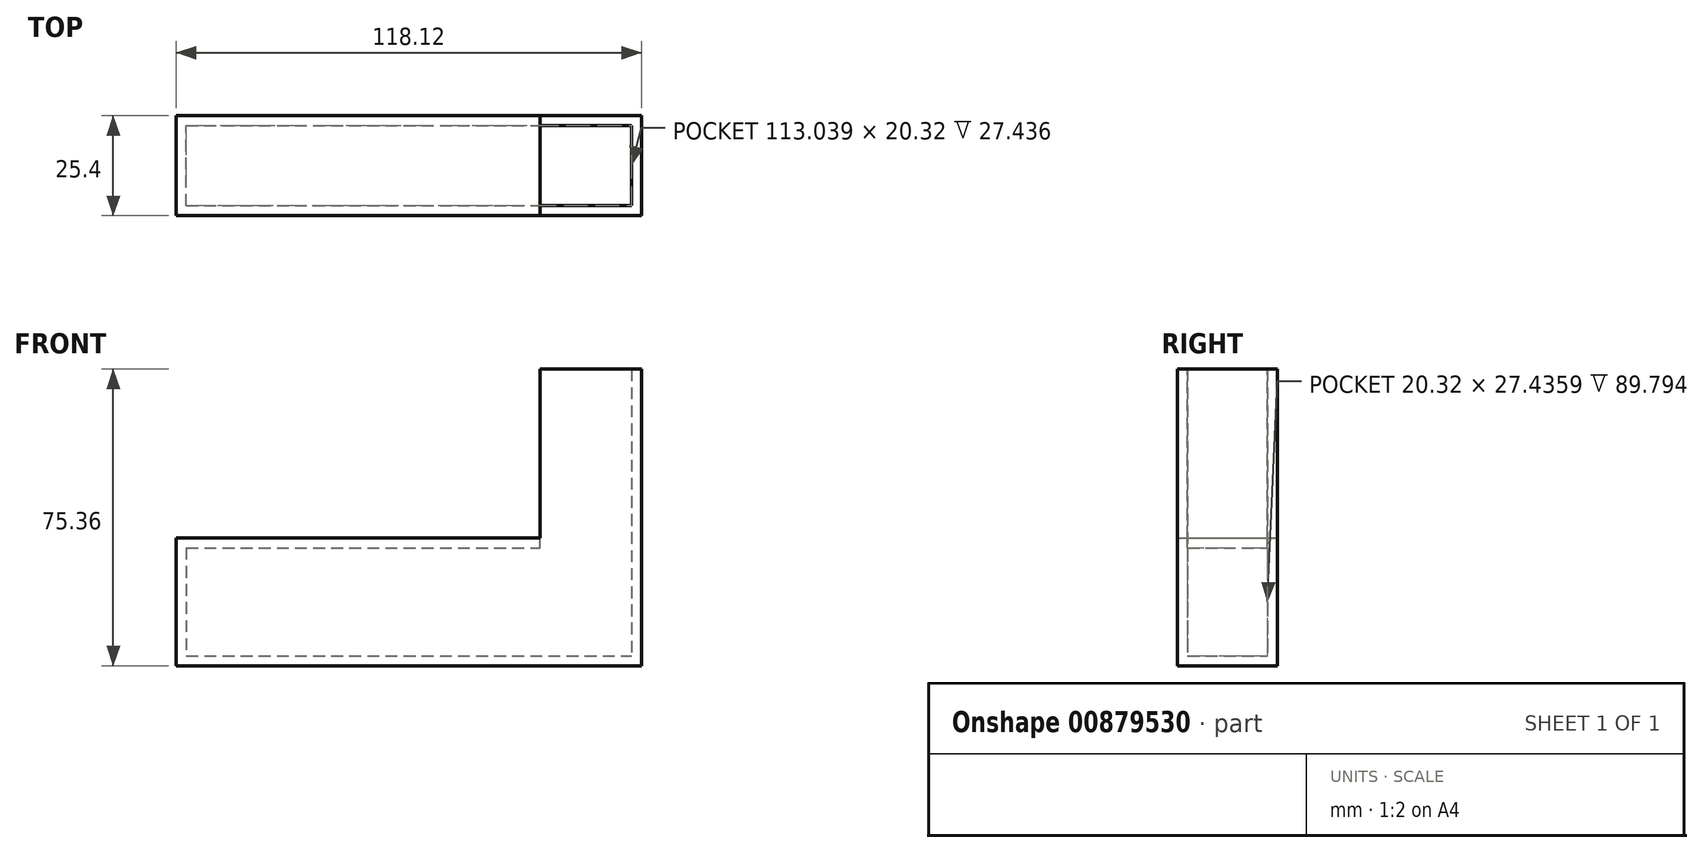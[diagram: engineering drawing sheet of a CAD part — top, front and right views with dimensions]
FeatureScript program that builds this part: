
annotation { "Feature Type Name" : "Feature", "Feature Type Description" : "" }
export const myFeature = defineFeature(function(context is Context, id is Id, definition is map)
    precondition{}
    {
        {
            var Q0;
            Q0=qCreatedBy(makeId("Front.planeOp"),FACE);
            var sketch = newSketch(context, id + "F0", { "sketchPlane" : qUnion([Q0])});
            skLineSegment(sketch, "E0.bottom", {"start": v(-56.22, 32.52) * mm, "end": v(61.9, 32.52) * mm});
            skLineSegment(sketch, "E0.top", {"start": v(-56.22, 0) * mm, "end": v(61.9, 0) * mm});
            skLineSegment(sketch, "E0.left", {"start": v(-56.22, 32.52) * mm, "end": v(-56.22, 0) * mm});
            skLineSegment(sketch, "E0.right", {"start": v(61.9, 32.52) * mm, "end": v(61.9, 0) * mm});
            skLineSegment(sketch, "E1", {"start": v(36.12, 32.52) * mm, "end": v(36.12, 49.96) * mm});
            skLineSegment(sketch, "E2", {"start": v(36.12, 49.96) * mm, "end": v(61.9, 49.96) * mm});
            skLineSegment(sketch, "E3", {"start": v(61.9, 49.96) * mm, "end": v(61.9, 32.52) * mm});
            skSolve(sketch);
        }
        {
            var Q0;
            Q0=makeQuery(id+"F0.imprint","IMPRINT",FACE,{"disambiguationData":[TD([[makeQuery(id+"F0.imprint","IMPRINT",EDGE,{"derivedFrom":sQuery(id+"F0.wireOp",EDGE,"E0.top")}),1.0]])]});
            var Q1;
            {var subQ2=sQuery(id+"F0.wireOp",EDGE,"E1");Q1=makeQuery(id+"F0.imprint","IMPRINT",FACE,{"disambiguationData":[TD([[makeQuery(id+"F0.imprint","IMPRINT",EDGE,{"derivedFrom":subQ2}),-1.0]])]});}
            extrude(context, id + "F1", {"entities" : qUnion([Q0, Q1]), "depth" : 25.4 * mm, "offsetDistance" : 25.4 * mm});
        }
        {
            var Q0;
            Q0=makeQuery(id+"F1.opExtrude","SWEPT_FACE",FACE,{"disambiguationData":[OSD([sQuery(id+"F0.wireOp",EDGE,"E2")])]});
            extrude(context, id + "F2", {"entities" : qUnion([Q0]), "operationType" : NewBodyOperationType.ADD, "depth" : 25.4 * mm, "offsetDistance" : 25.4 * mm});
        }
        {
            var Q0;
            Q0=makeQuery(id+"F2.opExtrude","CAP_FACE",FACE,{"disambiguationData":[OSD([sQuery(id+"F0.wireOp",EDGE,"E2")])],"isStart":false});
            var Q1;
            {var subQ0=sQuery(id+"F0.wireOp",EDGE,"E1");Q1=makeQuery(id+"F2.boolean.opBoolean","MERGE",FACE,{"derivedFrom":[makeQuery(id+"F1.opExtrude","SWEPT_FACE",FACE,{"disambiguationData":[OSD([subQ0])]}),makeQuery(id+"F2.opExtrude","SWEPT_FACE",FACE,{"disambiguationData":[OSD([subQ0,sQuery(id+"F0.wireOp",EDGE,"E2")])]})]});}
            shell(context, id + "F3", {"entities" : qUnion([Q0, Q1]), "thickness" : 2.54 * mm});
        }
    });
